# Revit family: Windows_Hajom_Architect_Type-SS
name_source: partatom
category: Windows
revit_build: Autodesk Revit 2018 (Build: 20170223_1515(x64)
units: mm (PartAtom-declared; Revit-internal decimal feet)

## family parameters
Always vertical = Yes
Cut with Voids When Loaded = No
Host = Wall
OmniClass Number = 23.30.20.00
OmniClass Title = Windows
Room Calculation Point = No
Shared = No

## types (1)
- Architect - Type SS
    AssetType = Fixed
    BIMObjectName = Windows_Hajom_Architect_Type-SS
    Brand = Hajom
    Category = Windows
    Default Sill Height = 800 mm  [stored 2.62467 ft]
    DurationUnit = Year
    Height = 0 mm  [stored 0 ft]
    Manufacturer = Hajom
    ManufacturerName = Hajom
    ManufacturerURL = https://www.hajom.com
    Material = Wood
    Model = Architect - Type SS
    NBSDescription = Wood window units
    NBSReference = 45-25-99/350
    Name = Architect_Type-SS
    NominalDepth = 105 mm  [stored 0.344488 ft]
    Revision = 1
    Rough Height = 0 mm  [stored 0 ft]
    Rough Width = 0 mm  [stored 0 ft]
    Shape = Rectangular
    Size = 380-780x380-1280x105 mm
    URL = https://www.hajom.com
    Uniclass2 = Pr_30_59_98
    Uniclass2015Description = Wood window units
    Uniclass2015Reference = Pr_30_59_98_96
    Version = 2
    VersionDate = 18/08/2022
    Wall Closure = By host
    WarrantyDurationUnit = Year
    Width = 0 mm  [stored 0 ft]

note: [stored X ft] marks values corroborated as IEEE doubles in the binary element streams (Revit-internal decimal feet)

## geometry (parser evidence)
native form markers: Sweep x29
no freeform markers — native parametric forms only
